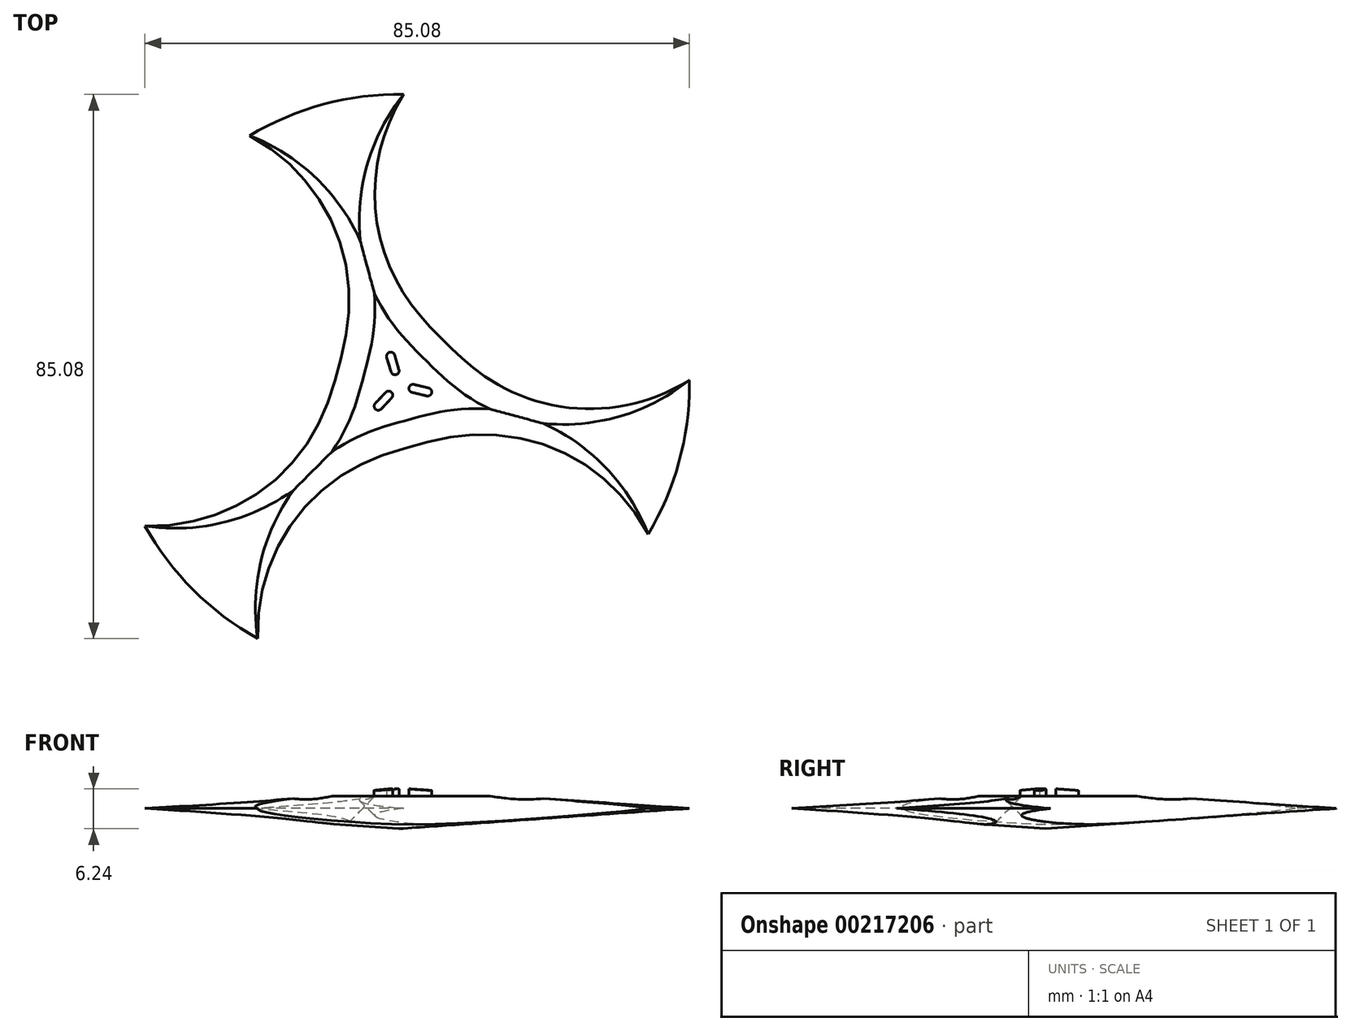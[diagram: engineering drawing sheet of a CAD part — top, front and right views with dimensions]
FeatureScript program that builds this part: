
annotation { "Feature Type Name" : "Feature", "Feature Type Description" : "" }
export const myFeature = defineFeature(function(context is Context, id is Id, definition is map)
    precondition{}
    {
        {
            var Q0;
            Q0=qCreatedBy(makeId("Front.planeOp"),FACE);
            var sketch = newSketch(context, id + "F0", { "sketchPlane" : qUnion([Q0])});
            skLineSegment(sketch, "E0", {"start": v(0, 0) * mm, "end": v(45.4, 3.18) * mm});
            skLineSegment(sketch, "E1", {"start": v(45.4, 3.18) * mm, "end": v(0, 6.35) * mm});
            skLineSegment(sketch, "E2", {"start": v(0, 6.35) * mm, "end": v(0, 0) * mm});
            skLineSegment(sketch, "E3", {"start": v(45.4, 3.18) * mm, "end": v(0, 3.18) * mm, "construction": true});
            skSolve(sketch);
        }
        {
            var Q0;
            Q0=makeQuery(id+"F0.imprint","IMPRINT",FACE,{"disambiguationData":[TD([[makeQuery(id+"F0.imprint","IMPRINT",EDGE,{"derivedFrom":sQuery(id+"F0.wireOp",EDGE,"E0")}),1.0]])]});
            var Q1;
            Q1=sQuery(id+"F0.wireOp",EDGE,"E2");
            revolve(context, id + "F1", {"entities" : qUnion([Q0]), "axis" : qUnion([Q1]), "revolveType" : RevolveType.FULL});
        }
        {
            var Q0;
            Q0=qCreatedBy(makeId("Top.planeOp"),FACE);
            var sketch = newSketch(context, id + "F2", { "sketchPlane" : qUnion([Q0])});
            skLineSegment(sketch, "E4", {"start": v(0, 0) * mm, "end": v(32.57, 0) * mm, "construction": true});
            skLineSegment(sketch, "E5", {"start": v(0, 0) * mm, "end": v(0, 29.15) * mm, "construction": true});
            skCircle(sketch, "E6", {"center": v(0, 0) * mm, "radius": 24.84 * mm});
            skLineSegment(sketch, "E7", {"start": v(0, 0) * mm, "end": v(25.4, 25.4) * mm, "construction": true});
            skCircle(sketch, "E8", {"center": v(25.4, 25.4) * mm, "radius": 25.4 * mm});
            skLineSegment(sketch, "E9.1.0", {"start": v(0, 0) * mm, "end": v(-25.24, -14.57) * mm, "construction": true});
            skCircle(sketch, "E9.1.1", {"center": v(-34.7, 9.3) * mm, "radius": 25.4 * mm});
            skLineSegment(sketch, "E9.2.0", {"start": v(0, 0) * mm, "end": v(25.24, -14.57) * mm, "construction": true});
            skCircle(sketch, "E9.2.1", {"center": v(9.3, -34.7) * mm, "radius": 25.4 * mm});
            skSolve(sketch);
        }
        {
            var Q0;
            Q0=qCreatedBy(makeId("Top.planeOp"),FACE);
            var sketch = newSketch(context, id + "F3", { "sketchPlane" : qUnion([Q0])});
            skCircle(sketch, "E10", {"center": v(0, 0) * mm, "radius": 11.9 * mm});
            skCircle(sketch, "E11", {"center": v(0, 0) * mm, "radius": 17.27 * mm});
            skSolve(sketch);
        }
        {
            var Q0;
            {var subQ0=sQuery(id+"F2.wireOp",EDGE,"E9.1.1");var subQ1=sQuery(id+"F2.wireOp",EDGE,"E6");var subQ2=makeQuery(id+"F2.imprint","INTERSECT",VERTEX,{"disambiguationData":[OD(0.0)],"derivedFrom":[subQ1,subQ0]});Q0=makeQuery(id+"F2.imprint","IMPRINT",FACE,{"disambiguationData":[TD([[makeQuery(id+"F2.imprint","IMPRINT",EDGE,{"disambiguationData":[TD([[subQ2,-1.0]])],"derivedFrom":subQ1}),-1.0]])]});}
            var Q1;
            {var subQ0=sQuery(id+"F2.wireOp",EDGE,"E8");var subQ1=sQuery(id+"F2.wireOp",EDGE,"E6");var subQ2=makeQuery(id+"F2.imprint","INTERSECT",VERTEX,{"disambiguationData":[OD(0.0)],"derivedFrom":[subQ1,subQ0]});Q1=makeQuery(id+"F2.imprint","IMPRINT",FACE,{"disambiguationData":[TD([[makeQuery(id+"F2.imprint","IMPRINT",EDGE,{"disambiguationData":[TD([[subQ2,1.0]])],"derivedFrom":subQ1}),-1.0]])]});}
            var Q2;
            {var subQ0=sQuery(id+"F2.wireOp",EDGE,"E9.2.1");var subQ1=sQuery(id+"F2.wireOp",EDGE,"E6");var subQ2=makeQuery(id+"F2.imprint","INTERSECT",VERTEX,{"disambiguationData":[OD(0.0)],"derivedFrom":[subQ1,subQ0]});Q2=makeQuery(id+"F2.imprint","IMPRINT",FACE,{"disambiguationData":[TD([[makeQuery(id+"F2.imprint","IMPRINT",EDGE,{"disambiguationData":[TD([[subQ2,-1.0]])],"derivedFrom":subQ1}),-1.0]])]});}
            var Q3;
            {var subQ0=sQuery(id+"F2.wireOp",EDGE,"E8");var subQ1=sQuery(id+"F2.wireOp",EDGE,"E6");var subQ2=makeQuery(id+"F2.imprint","INTERSECT",VERTEX,{"disambiguationData":[OD(0.0)],"derivedFrom":[subQ1,subQ0]});Q3=makeQuery(id+"F2.imprint","IMPRINT",FACE,{"disambiguationData":[TD([[makeQuery(id+"F2.imprint","IMPRINT",EDGE,{"disambiguationData":[TD([[subQ2,1.0]])],"derivedFrom":subQ1}),1.0]])]});}
            var Q4;
            {var subQ0=sQuery(id+"F2.wireOp",EDGE,"E9.1.1");var subQ1=sQuery(id+"F2.wireOp",EDGE,"E6");var subQ2=makeQuery(id+"F2.imprint","INTERSECT",VERTEX,{"disambiguationData":[OD(0.0)],"derivedFrom":[subQ1,subQ0]});Q4=makeQuery(id+"F2.imprint","IMPRINT",FACE,{"disambiguationData":[TD([[makeQuery(id+"F2.imprint","IMPRINT",EDGE,{"disambiguationData":[TD([[subQ2,-1.0]])],"derivedFrom":subQ1}),1.0]])]});}
            var Q5;
            {var subQ0=sQuery(id+"F2.wireOp",EDGE,"E9.2.1");var subQ1=sQuery(id+"F2.wireOp",EDGE,"E6");var subQ2=makeQuery(id+"F2.imprint","INTERSECT",VERTEX,{"disambiguationData":[OD(0.0)],"derivedFrom":[subQ1,subQ0]});Q5=makeQuery(id+"F2.imprint","IMPRINT",FACE,{"disambiguationData":[TD([[makeQuery(id+"F2.imprint","IMPRINT",EDGE,{"disambiguationData":[TD([[subQ2,-1.0]])],"derivedFrom":subQ1}),1.0]])]});}
            extrude(context, id + "F4", {"entities" : qUnion([Q0, Q1, Q2, Q3, Q4, Q5]), "operationType" : NewBodyOperationType.REMOVE, "oppositeDirection" : true, "depth" : 6.1 * mm, "hasSecondDirection" : true, "secondDirectionOppositeDirection" : false, "secondDirectionDepth" : 26.67 * mm});
        }
        {
            var Q0;
            Q0=makeQuery(id+"F4.boolean.opBoolean","INTERSECT",EDGE,{"derivedFrom":[makeQuery(id+"F1.opRevolve","SWEPT_FACE",FACE,{"disambiguationData":[OSD([sQuery(id+"F0.wireOp",EDGE,"E1")])]}),makeQuery(id+"F4.opExtrude","SWEPT_FACE",FACE,{"disambiguationData":[OSD([sQuery(id+"F2.wireOp",EDGE,"E8")])]})]});
            var Q1;
            Q1=makeQuery(id+"F4.boolean.opBoolean","INTERSECT",EDGE,{"derivedFrom":[makeQuery(id+"F1.opRevolve","SWEPT_FACE",FACE,{"disambiguationData":[OSD([sQuery(id+"F0.wireOp",EDGE,"E1")])]}),makeQuery(id+"F4.opExtrude","SWEPT_FACE",FACE,{"disambiguationData":[OSD([sQuery(id+"F2.wireOp",EDGE,"E9.1.1")])]})]});
            var Q2;
            Q2=makeQuery(id+"F4.boolean.opBoolean","INTERSECT",EDGE,{"derivedFrom":[makeQuery(id+"F1.opRevolve","SWEPT_FACE",FACE,{"disambiguationData":[OSD([sQuery(id+"F0.wireOp",EDGE,"E1")])]}),makeQuery(id+"F4.opExtrude","SWEPT_FACE",FACE,{"disambiguationData":[OSD([sQuery(id+"F2.wireOp",EDGE,"E9.2.1")])]})]});
            chamfer(context, id + "F5", {"entities" : qUnion([Q0, Q1, Q2]), "width" : 6.1 * mm, "tangentPropagation" : true});
        }
        {
            var Q0;
            Q0=makeQuery(id+"F3.imprint","IMPRINT",FACE,{"disambiguationData":[TD([[makeQuery(id+"F3.imprint","IMPRINT",EDGE,{"derivedFrom":sQuery(id+"F3.wireOp",EDGE,"E10")}),-1.0]])]});
            cPlane(context, id + "F6", {"entities" : qUnion([Q0]), "cplaneType" : CPlaneType.OFFSET, "offset" : 5.08 * mm, "width" : 152.4 * mm, "height" : 152.4 * mm});
        }
        {
            var Q0;
            Q0=qCreatedBy(id+"F6.planeOp",FACE);
            var sketch = newSketch(context, id + "F7", { "sketchPlane" : qUnion([Q0])});
            skCircle(sketch, "E12", {"center": v(0, 0) * mm, "radius": 16.8 * mm});
            skLineSegment(sketch, "E13", {"start": v(-0.6, 2.2) * mm, "end": v(-1.29, 4.47) * mm});
            skLineSegment(sketch, "E14.1.0", {"start": v(-1.6, -1.62) * mm, "end": v(-3.23, -3.35) * mm});
            skLineSegment(sketch, "E14.2.0", {"start": v(2.2, -0.58) * mm, "end": v(4.51, -1.12) * mm});
            skArc(sketch, "E15.0.startCap", {"start": v(0, 2.38) * mm, "mid": v(-0.42, 1.59) * mm, "end": v(-1.21, 2.01) * mm});
            skArc(sketch, "E15.0.endCap", {"start": v(-1.9, 4.29) * mm, "mid": v(-1.47, 5.08) * mm, "end": v(-0.68, 4.65) * mm});
            skLineSegment(sketch, "E15.0.left", {"start": v(-1.21, 2.01) * mm, "end": v(-1.9, 4.29) * mm});
            skLineSegment(sketch, "E15.0.right", {"start": v(0, 2.38) * mm, "end": v(-0.68, 4.65) * mm});
            skArc(sketch, "E15.1.startCap", {"start": v(2.06, -1.2) * mm, "mid": v(1.59, -0.43) * mm, "end": v(2.35, 0.04) * mm});
            skArc(sketch, "E15.1.endCap", {"start": v(4.66, -0.5) * mm, "mid": v(5.13, -1.27) * mm, "end": v(4.37, -1.74) * mm});
            skLineSegment(sketch, "E15.1.left", {"start": v(2.35, 0.04) * mm, "end": v(4.66, -0.5) * mm});
            skLineSegment(sketch, "E15.1.right", {"start": v(2.06, -1.2) * mm, "end": v(4.37, -1.74) * mm});
            skArc(sketch, "E15.2.startCap", {"start": v(-2.06, -1.19) * mm, "mid": v(-1.17, -1.16) * mm, "end": v(-1.14, -2.06) * mm});
            skArc(sketch, "E15.2.endCap", {"start": v(-2.77, -3.78) * mm, "mid": v(-3.66, -3.81) * mm, "end": v(-3.7, -2.91) * mm});
            skLineSegment(sketch, "E15.2.left", {"start": v(-1.14, -2.06) * mm, "end": v(-2.77, -3.78) * mm});
            skLineSegment(sketch, "E15.2.right", {"start": v(-2.06, -1.19) * mm, "end": v(-3.7, -2.91) * mm});
            skSolve(sketch);
        }
        {
            var Q0;
            Q0=makeQuery(id+"F7.imprint","IMPRINT",FACE,{"disambiguationData":[TD([[makeQuery(id+"F7.imprint","IMPRINT",EDGE,{"derivedFrom":sQuery(id+"F7.wireOp",EDGE,"E12")}),1.0]])]});
            var Q1;
            Q1=makeQuery(id+"F7.imprint","IMPRINT",FACE,{"disambiguationData":[TD([[makeQuery(id+"F7.imprint","IMPRINT",EDGE,{"derivedFrom":sQuery(id+"F7.wireOp",EDGE,"E15.0.startCap")}),-1.0]])]});
            var Q2;
            Q2=makeQuery(id+"F7.imprint","IMPRINT",FACE,{"disambiguationData":[TD([[makeQuery(id+"F7.imprint","IMPRINT",EDGE,{"derivedFrom":sQuery(id+"F7.wireOp",EDGE,"E15.2.startCap")}),-1.0]])]});
            var Q3;
            Q3=makeQuery(id+"F7.imprint","IMPRINT",FACE,{"disambiguationData":[TD([[makeQuery(id+"F7.imprint","IMPRINT",EDGE,{"derivedFrom":sQuery(id+"F7.wireOp",EDGE,"E15.1.startCap")}),-1.0]])]});
            extrude(context, id + "F8", {"entities" : qUnion([Q0, Q1, Q2, Q3]), "operationType" : NewBodyOperationType.REMOVE, "depth" : 15.5 * mm, "hasSecondDirection" : true, "secondDirectionOppositeDirection" : false, "secondDirectionDepth" : 0.05 * mm});
        }
    });
